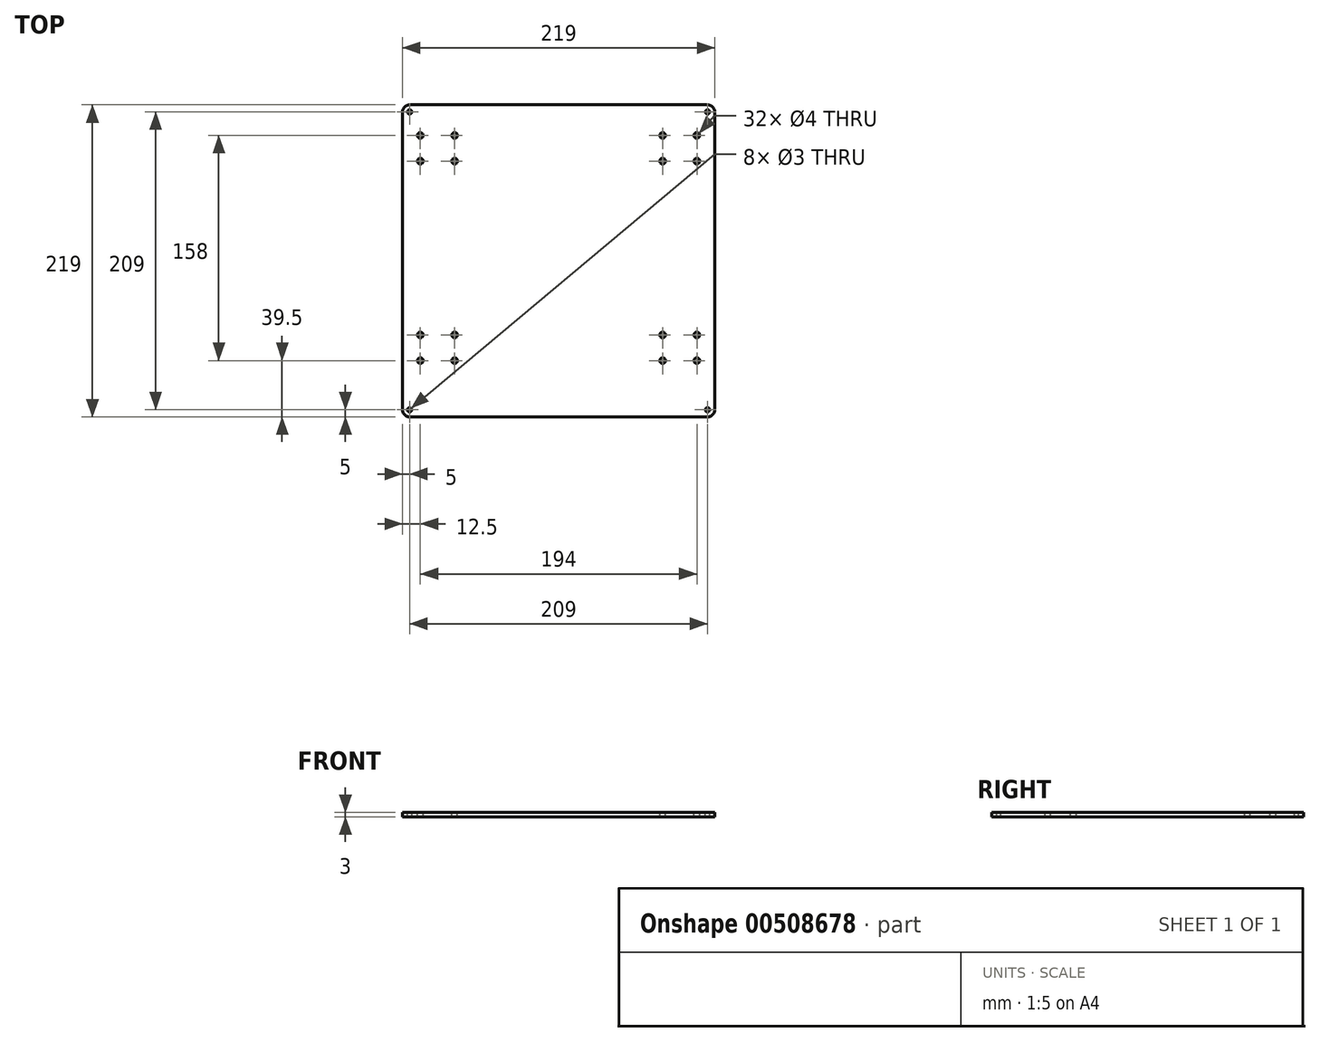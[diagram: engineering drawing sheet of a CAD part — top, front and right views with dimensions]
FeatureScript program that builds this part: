
annotation { "Feature Type Name" : "Feature", "Feature Type Description" : "" }
export const myFeature = defineFeature(function(context is Context, id is Id, definition is map)
    precondition{}
    {
        {
            var Q0;
            Q0=qCreatedBy(makeId("Top.planeOp"),FACE);
            var sketch = newSketch(context, id + "F0", { "sketchPlane" : qUnion([Q0])});
            skLineSegment(sketch, "E0.bottom", {"start": v(109.5, -109.5) * mm, "end": v(-109.5, -109.5) * mm});
            skLineSegment(sketch, "E0.top", {"start": v(109.5, 109.5) * mm, "end": v(-109.5, 109.5) * mm});
            skLineSegment(sketch, "E0.left", {"start": v(109.5, -109.5) * mm, "end": v(109.5, 109.5) * mm});
            skLineSegment(sketch, "E0.right", {"start": v(-109.5, -109.5) * mm, "end": v(-109.5, 109.5) * mm});
            skPoint(sketch, "E0.middle", {"position": v(0, 0) * mm});
            skSolve(sketch);
        }
        {
            var Q0;
            Q0 = qSketchRegion(id + "F0", true);
            extrude(context, id + "F1", {"entities" : qUnion([Q0]), "depth" : 3 * mm});
        }
        {
            var Q0;
            Q0=makeQuery(id+"F1.opExtrude","SWEPT_EDGE",EDGE,{"disambiguationData":[OSD([sQuery(id+"F0.wireOp",EDGE,"E0.bottom"),sQuery(id+"F0.wireOp",EDGE,"E0.left")])]});
            var Q1;
            Q1=makeQuery(id+"F1.opExtrude","SWEPT_EDGE",EDGE,{"disambiguationData":[OSD([sQuery(id+"F0.wireOp",EDGE,"E0.top"),sQuery(id+"F0.wireOp",EDGE,"E0.left")])]});
            var Q2;
            Q2=makeQuery(id+"F1.opExtrude","SWEPT_EDGE",EDGE,{"disambiguationData":[OSD([sQuery(id+"F0.wireOp",EDGE,"E0.top"),sQuery(id+"F0.wireOp",EDGE,"E0.right")])]});
            var Q3;
            Q3=makeQuery(id+"F1.opExtrude","SWEPT_EDGE",EDGE,{"disambiguationData":[OSD([sQuery(id+"F0.wireOp",EDGE,"E0.bottom"),sQuery(id+"F0.wireOp",EDGE,"E0.right")])]});
            fillet(context, id + "F2", {"entities" : qUnion([Q0, Q1, Q2, Q3]), "radius" : 5 * mm, "tangentPropagation" : true, "allowEdgeOverflow" : false});
        }
        {
            var Q0;
            Q0=makeQuery(id+"F1.opExtrude","CAP_FACE",FACE,{"disambiguationData":[OSD([sQuery(id+"F0.wireOp",EDGE,"E0.bottom"),sQuery(id+"F0.wireOp",EDGE,"E0.top"),sQuery(id+"F0.wireOp",EDGE,"E0.left"),sQuery(id+"F0.wireOp",EDGE,"E0.right")])],"isStart":false});
            var sketch = newSketch(context, id + "F3", { "sketchPlane" : qUnion([Q0])});
            skPoint(sketch, "E1", {"position": v(-104.5, -104.5) * mm});
            skPoint(sketch, "E2", {"position": v(104.5, -104.5) * mm});
            skPoint(sketch, "E3", {"position": v(104.5, 104.5) * mm});
            skPoint(sketch, "E4", {"position": v(-104.5, 104.5) * mm});
            skSolve(sketch);
        }
        {
            var Q0;
            Q0=sQuery(id+"F3.wireOp",VERTEX,"E1");
            var Q1;
            Q1=sQuery(id+"F3.wireOp",VERTEX,"E2");
            var Q2;
            Q2=sQuery(id+"F3.wireOp",VERTEX,"E3");
            var Q3;
            Q3=sQuery(id+"F3.wireOp",VERTEX,"E4");
            var Q4;
            Q4=makeQuery(id+"F1.opExtrude","SWEPT_BODY",BODY,{"disambiguationData":[OSD([sQuery(id+"F0.wireOp",EDGE,"E0.bottom"),sQuery(id+"F0.wireOp",EDGE,"E0.top"),sQuery(id+"F0.wireOp",EDGE,"E0.left"),sQuery(id+"F0.wireOp",EDGE,"E0.right")])]});
            hole(context, id + "F4", {"style" : HoleStyle.SIMPLE, "endStyle" : HoleEndStyle.THROUGH, "holeDiameter" : 3 * mm, "isTappedThrough" : true, "tappedDepth" : 12 * mm, "tapClearance" : 3, "startFromSketch" : true, "locations" : qUnion([Q0, Q1, Q2, Q3]), "scope" : qUnion([Q4])});
        }
        {
            var Q0;
            Q0=makeQuery(id+"F1.opExtrude","CAP_FACE",FACE,{"disambiguationData":[OSD([sQuery(id+"F0.wireOp",EDGE,"E0.bottom"),sQuery(id+"F0.wireOp",EDGE,"E0.top"),sQuery(id+"F0.wireOp",EDGE,"E0.left"),sQuery(id+"F0.wireOp",EDGE,"E0.right")])],"isStart":false});
            var sketch = newSketch(context, id + "F5", { "sketchPlane" : qUnion([Q0])});
            skPoint(sketch, "E5", {"position": v(-97, 88) * mm});
            skPoint(sketch, "E6", {"position": v(-73, 88) * mm});
            skPoint(sketch, "E7", {"position": v(-73, 70) * mm});
            skPoint(sketch, "E8", {"position": v(-97, 70) * mm});
            skPoint(sketch, "E9", {"position": v(-97, -52) * mm});
            skPoint(sketch, "E10", {"position": v(-97, -70) * mm});
            skPoint(sketch, "E11", {"position": v(-73, -70) * mm});
            skPoint(sketch, "E12", {"position": v(-73, -52) * mm});
            skPoint(sketch, "E13", {"position": v(73, -52) * mm});
            skPoint(sketch, "E14", {"position": v(73, -70) * mm});
            skPoint(sketch, "E15", {"position": v(97, -70) * mm});
            skPoint(sketch, "E16", {"position": v(97, -52) * mm});
            skPoint(sketch, "E17", {"position": v(97, 70) * mm});
            skPoint(sketch, "E18", {"position": v(97, 88) * mm});
            skPoint(sketch, "E19", {"position": v(73, 88) * mm});
            skPoint(sketch, "E20", {"position": v(73, 70) * mm});
            skSolve(sketch);
        }
        {
            var Q0;
            Q0=sQuery(id+"F5.wireOp",VERTEX,"E10");
            var Q1;
            Q1=sQuery(id+"F5.wireOp",VERTEX,"E11");
            var Q2;
            Q2=sQuery(id+"F5.wireOp",VERTEX,"E12");
            var Q3;
            Q3=sQuery(id+"F5.wireOp",VERTEX,"E9");
            var Q4;
            Q4=sQuery(id+"F5.wireOp",VERTEX,"E8");
            var Q5;
            Q5=sQuery(id+"F5.wireOp",VERTEX,"E7");
            var Q6;
            Q6=sQuery(id+"F5.wireOp",VERTEX,"E6");
            var Q7;
            Q7=sQuery(id+"F5.wireOp",VERTEX,"E5");
            var Q8;
            Q8=sQuery(id+"F5.wireOp",VERTEX,"E19");
            var Q9;
            Q9=sQuery(id+"F5.wireOp",VERTEX,"E20");
            var Q10;
            Q10=sQuery(id+"F5.wireOp",VERTEX,"E17");
            var Q11;
            Q11=sQuery(id+"F5.wireOp",VERTEX,"E18");
            var Q12;
            Q12=sQuery(id+"F5.wireOp",VERTEX,"E16");
            var Q13;
            Q13=sQuery(id+"F5.wireOp",VERTEX,"E15");
            var Q14;
            Q14=sQuery(id+"F5.wireOp",VERTEX,"E14");
            var Q15;
            Q15=sQuery(id+"F5.wireOp",VERTEX,"E13");
            var Q16;
            Q16=makeQuery(id+"F1.opExtrude","SWEPT_BODY",BODY,{"disambiguationData":[OSD([sQuery(id+"F0.wireOp",EDGE,"E0.bottom"),sQuery(id+"F0.wireOp",EDGE,"E0.top"),sQuery(id+"F0.wireOp",EDGE,"E0.left"),sQuery(id+"F0.wireOp",EDGE,"E0.right")])]});
            hole(context, id + "F6", {"style" : HoleStyle.SIMPLE, "endStyle" : HoleEndStyle.THROUGH, "holeDiameter" : 4 * mm, "isTappedThrough" : true, "tappedDepth" : 12 * mm, "tapClearance" : 3, "startFromSketch" : true, "locations" : qUnion([Q0, Q1, Q2, Q3, Q4, Q5, Q6, Q7, Q8, Q9, Q10, Q11, Q12, Q13, Q14, Q15]), "scope" : qUnion([Q16])});
        }
    });
